# Revit family: Franke_Card_reader-A600_A800_A1000(EU)
name_source: partatom
category: Specialty Equipment
revit_build: Autodesk Revit 2015 (Build: 20140606_1530(x64)
units: mm (PartAtom-declared; Revit-internal decimal feet)

## types (2) — shared parameters
Assembly Code = key module - payment systems
Cycle = 50 Hz
Cycle Alternative = 60 Hz
Depth (mm) = 452 mm  [stored 1.48294 ft]
Description = payment systems key module - card reader
Energy loss acc. to DIN 18873 = -
Height (mm) = 585 mm  [stored 1.91929 ft]
Keynote = key module - payment systems
Manufacturer = Franke
Max Overcurrent Protection = 10 A
Model = 410906 - Card reader-A600, A800, A1000
Number of Nutral Conductors = 1
Number of Poles = 1
Number of Protective Conductors = 1
URL = https://www.franke.com
Volts max. = 264 V
Volts min. = 85 V
Watts = system dependent
Weight = 18 kg
Width (mm) = 200 mm  [stored 0.656168 ft]
zero-valued in all types: Cost

## per-type parameters (varying)
| type | Frontcover |
| Card reader-A600,A800,A1000(85-264V/black line/EU) | Franke Black |
| Card reader-A600,A800,A1000(85-264V/anthracite/EU) | Franke Anthracite |

note: [stored X ft] marks values corroborated as IEEE doubles in the binary element streams (Revit-internal decimal feet)
